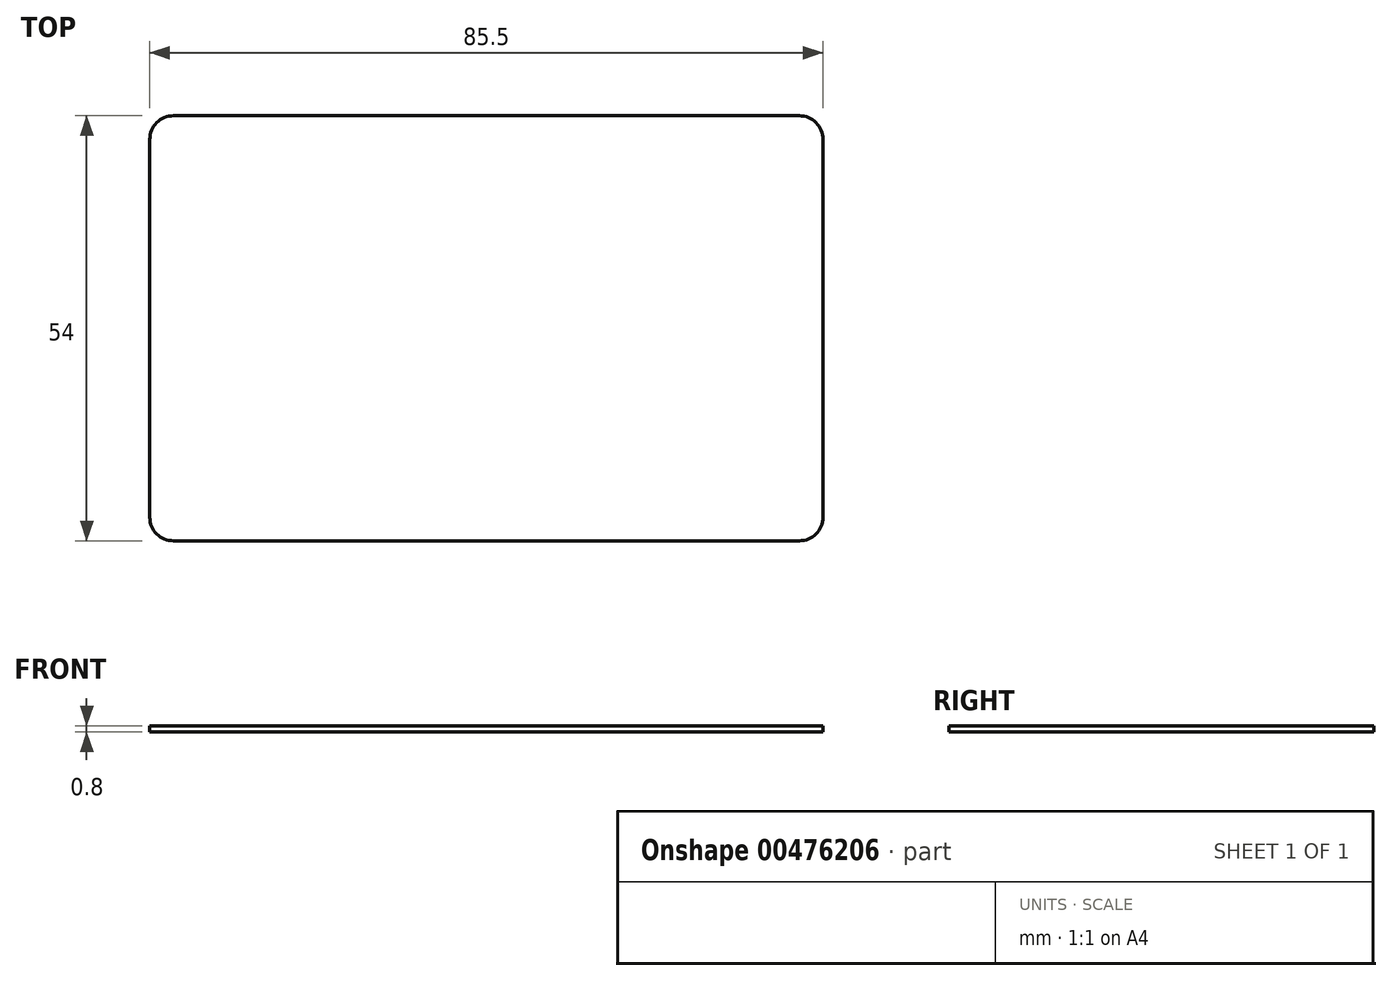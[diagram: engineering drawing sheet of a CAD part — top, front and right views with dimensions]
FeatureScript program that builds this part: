
annotation { "Feature Type Name" : "Feature", "Feature Type Description" : "" }
export const myFeature = defineFeature(function(context is Context, id is Id, definition is map)
    precondition{}
    {
        {
            var Q0;
            Q0=qCreatedBy(makeId("Top.planeOp"),FACE);
            var sketch = newSketch(context, id + "F0", { "sketchPlane" : qUnion([Q0])});
            skLineSegment(sketch, "E0.bottom", {"start": v(42.75, -27) * mm, "end": v(-42.75, -27) * mm});
            skLineSegment(sketch, "E0.top", {"start": v(42.75, 27) * mm, "end": v(-42.75, 27) * mm});
            skLineSegment(sketch, "E0.left", {"start": v(42.75, -27) * mm, "end": v(42.75, 27) * mm});
            skLineSegment(sketch, "E0.right", {"start": v(-42.75, -27) * mm, "end": v(-42.75, 27) * mm});
            skPoint(sketch, "E0.middle", {"position": v(0, 0) * mm});
            skSolve(sketch);
        }
        {
            var Q0;
            Q0=makeQuery(id+"F0.imprint","IMPRINT",FACE,{"disambiguationData":[TD([[makeQuery(id+"F0.imprint","IMPRINT",EDGE,{"derivedFrom":sQuery(id+"F0.wireOp",EDGE,"E0.bottom")}),-1.0]])]});
            extrude(context, id + "F1", {"entities" : qUnion([Q0]), "depth" : .8 * mm});
        }
        {
            var Q0;
            Q0=makeQuery(id+"F1.opExtrude","SWEPT_EDGE",EDGE,{"disambiguationData":[OSD([sQuery(id+"F0.wireOp",EDGE,"E0.bottom"),sQuery(id+"F0.wireOp",EDGE,"E0.right")])]});
            var Q1;
            Q1=makeQuery(id+"F1.opExtrude","SWEPT_EDGE",EDGE,{"disambiguationData":[OSD([sQuery(id+"F0.wireOp",EDGE,"E0.top"),sQuery(id+"F0.wireOp",EDGE,"E0.left")])]});
            var Q2;
            Q2=makeQuery(id+"F1.opExtrude","SWEPT_EDGE",EDGE,{"disambiguationData":[OSD([sQuery(id+"F0.wireOp",EDGE,"E0.top"),sQuery(id+"F0.wireOp",EDGE,"E0.right")])]});
            var Q3;
            Q3=makeQuery(id+"F1.opExtrude","SWEPT_EDGE",EDGE,{"disambiguationData":[OSD([sQuery(id+"F0.wireOp",EDGE,"E0.bottom"),sQuery(id+"F0.wireOp",EDGE,"E0.left")])]});
            fillet(context, id + "F2", {"entities" : qUnion([Q0, Q1, Q2, Q3]), "radius" : 3 * mm, "tangentPropagation" : true, "allowEdgeOverflow" : false});
        }
    });
